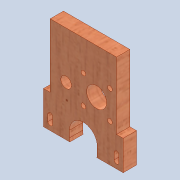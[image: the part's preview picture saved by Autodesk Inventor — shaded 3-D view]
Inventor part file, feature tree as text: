
AUTODESK INVENTOR PART (.ipt)
format: ipt  version: 2020 (Build 240168000, 168)  size: 231,424 bytes
history: native  units: mm
features: extrude x6, sketch x3, other x3, direct_edit x1, reference x1, move_body x1
ambient origin geometry x8: Origin, YZ Plane, XZ Plane, XY Plane, X Axis, Y Axis, Z Axis, Center Point
bodies: Solid1 (feature_tree)
feature tree (15):
  extrude  "Extrusion1"  Depth=60.0mm
  extrude  "Extrusion4"  Depth=10.0mm TaperAngle=0.0deg
  extrude  "Extrusion5"  TaperAngle=0.0deg  [1 undecoded]
  extrude  "Extrusion6"  TaperAngle=0.0deg  [1 undecoded]
  extrude  "Extrusion7"  Depth=5.0mm
  extrude  "Extrusion8"  Depth=5.0mm
  direct_edit  "Direct Edit1"
  sketch  "Sketch1"  dims[d0=60.0mm d1=65.0mm]
  sketch  "Sketch7"  dims[d2=10.0mm d3=0.0mm d11=10.0mm d12=0.0mm]
  reference  "Reference6"
  sketch  "Sketch8"  dims[d13=15.0mm d14=0.0mm d15=0.0mm d16=0.0mm d17=0.0mm d18=5.0mm d19=5.0mm d20=0.0mm d21=0.0mm d22=5.0mm d23=3.5mm d24=5.0mm d25=10.5mm d26=7.5mm d27=30.0mm d28=25.608627mm d29=20.0mm d31=21.5mm d33=3.5mm d35=8.0mm d36=17.0mm d37=27.469095mm d38=10.0mm d39=0.0mm d42=20.0mm d43=40.0mm d44=0.0mm d45=0.0mm d46=8.0mm]
  parser-record x1  (decoder bookkeeping rows leaked as tree rows — omitted from the tree; the rows remain in map.json)
  other  "0005-00-00 Ansamblu_General.iam"
  other  "0005-10-002 Suport1 Seringa.ipt:8"
  move_body  "Move1"
note: 2 required parameter values undecoded (feature->parameter linkage not recoverable at this tier; creation-order binding heuristic only, values carry confidence <= 0.55)
note: 1 file-system path scrubbed to <path> (originals preserved in map.json)
